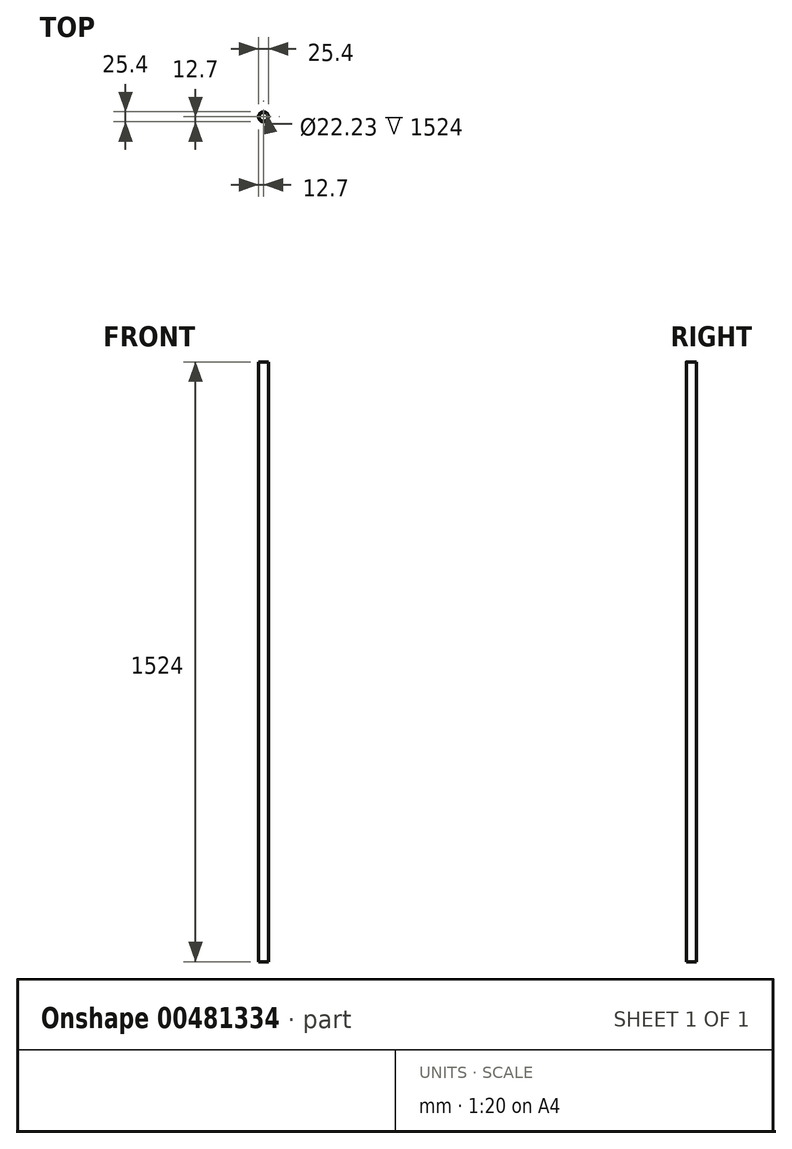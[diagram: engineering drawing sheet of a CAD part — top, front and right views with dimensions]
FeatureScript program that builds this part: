
annotation { "Feature Type Name" : "Feature", "Feature Type Description" : "" }
export const myFeature = defineFeature(function(context is Context, id is Id, definition is map)
    precondition{}
    {
        {
            var Q0;
            Q0=qCreatedBy(makeId("Top.planeOp"),FACE);
            var sketch = newSketch(context, id + "F0", { "sketchPlane" : qUnion([Q0])});
            skCircle(sketch, "E0", {"center": v(0, 0) * mm, "radius": 12.7 * mm});
            skCircle(sketch, "E1", {"center": v(0, 0) * mm, "radius": 11.11 * mm});
            skSolve(sketch);
        }
        {
            var Q0;
            Q0 = qSketchRegion(id + "F0", true);
            extrude(context, id + "F1", {"entities" : qUnion([Q0]), "depth" : 1524 * mm});
        }
    });
